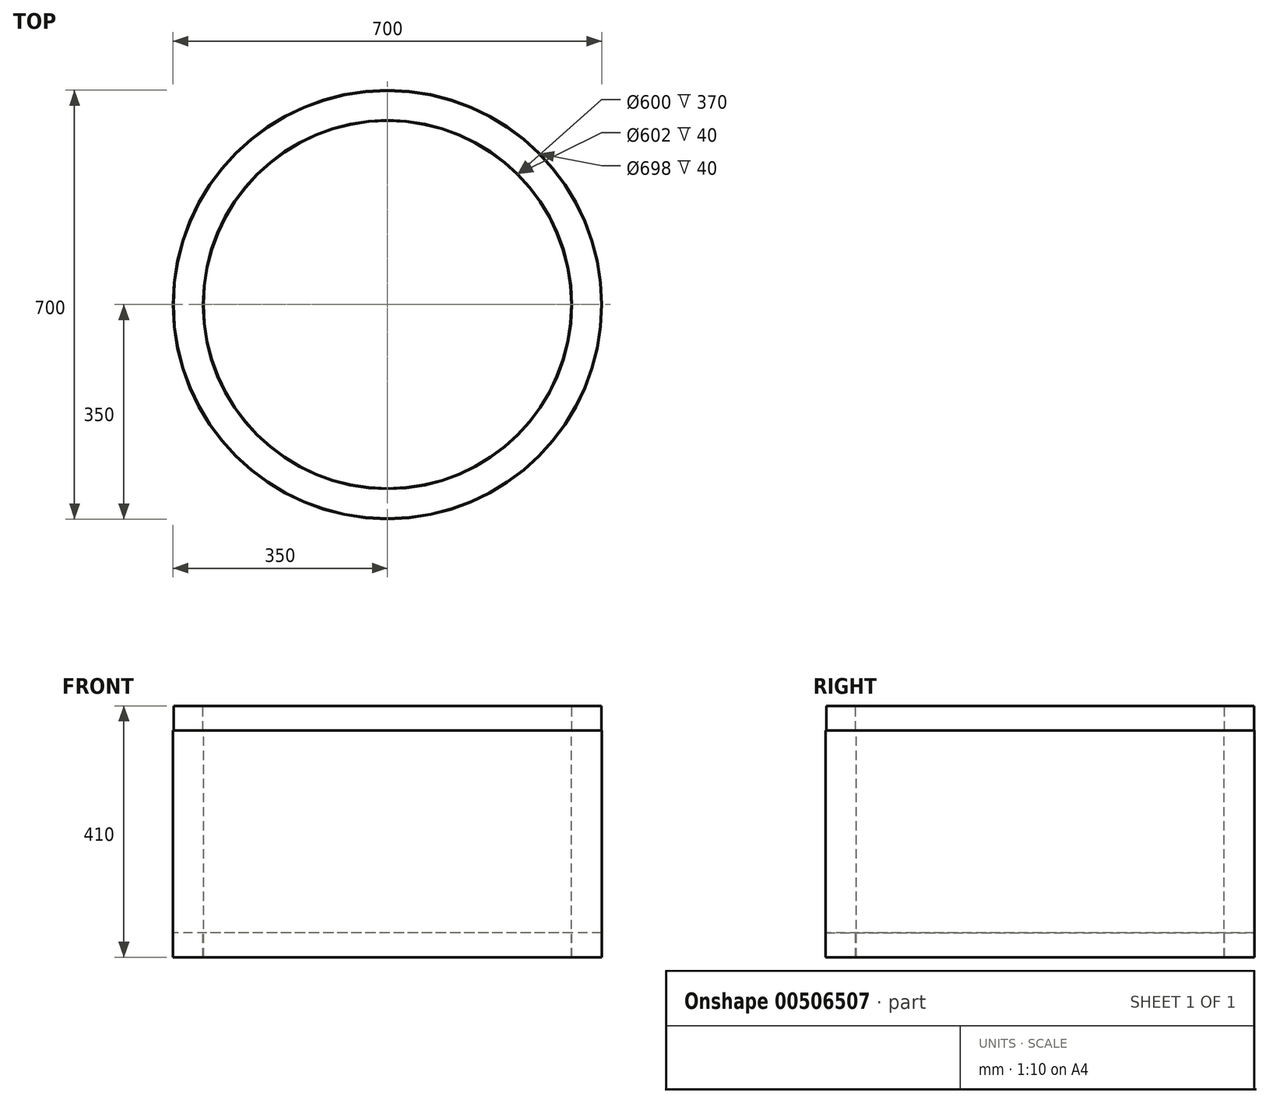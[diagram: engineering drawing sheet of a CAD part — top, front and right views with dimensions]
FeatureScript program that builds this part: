
annotation { "Feature Type Name" : "Feature", "Feature Type Description" : "" }
export const myFeature = defineFeature(function(context is Context, id is Id, definition is map)
    precondition{}
    {
        {
            var Q0;
            Q0=qCreatedBy(makeId("Front.planeOp"),FACE);
            var sketch = newSketch(context, id + "F0", { "sketchPlane" : qUnion([Q0])});
            skLineSegment(sketch, "E0", {"start": v(0, 74.87) * mm, "end": v(0, -73.71) * mm, "construction": true});
            skLineSegment(sketch, "E1", {"start": v(0, 374.84) * mm, "end": v(0, -528.94) * mm, "construction": true});
            skLineSegment(sketch, "E2", {"start": v(-300, -489.75) * mm, "end": v(-300, -119.75) * mm});
            skLineSegment(sketch, "E3", {"start": v(-300, -119.75) * mm, "end": v(-301, -119.75) * mm});
            skLineSegment(sketch, "E4", {"start": v(-301, -119.75) * mm, "end": v(-301, -79.75) * mm});
            skLineSegment(sketch, "E5", {"start": v(-301, -79.75) * mm, "end": v(-349, -79.75) * mm});
            skLineSegment(sketch, "E6", {"start": v(-349, -79.75) * mm, "end": v(-349, -119.75) * mm});
            skLineSegment(sketch, "E7", {"start": v(-349, -119.75) * mm, "end": v(-350, -119.75) * mm});
            skLineSegment(sketch, "E8", {"start": v(-350, -119.75) * mm, "end": v(-350, -489.75) * mm});
            skLineSegment(sketch, "E9", {"start": v(-350, -489.75) * mm, "end": v(-349, -489.75) * mm});
            skLineSegment(sketch, "E10", {"start": v(-349, -489.75) * mm, "end": v(-349, -449.75) * mm});
            skLineSegment(sketch, "E11", {"start": v(-349, -449.75) * mm, "end": v(-301, -449.75) * mm});
            skLineSegment(sketch, "E12", {"start": v(-301, -449.75) * mm, "end": v(-301, -489.75) * mm});
            skLineSegment(sketch, "E13", {"start": v(-301, -489.75) * mm, "end": v(-300, -489.75) * mm});
            skSolve(sketch);
        }
        {
            var Q0;
            Q0=qSketchRegion(id+"F0",true);
            var Q1;
            Q1=sQuery(id+"F0.wireOp",EDGE,"E1");
            revolve(context, id + "F1", {"entities" : qUnion([Q0]), "axis" : qUnion([Q1]), "revolveType" : RevolveType.FULL});
        }
    });
